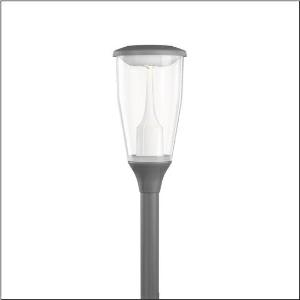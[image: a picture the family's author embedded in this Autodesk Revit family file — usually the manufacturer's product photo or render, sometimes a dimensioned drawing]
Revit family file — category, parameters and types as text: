
# Revit family: dl_11_iq___p1_0a_5xa5575lf14h000022_ea02
name_source: partatom
category: Lighting Fixtures
units: mm (PartAtom-declared; Revit-internal decimal feet)

## family parameters
Cut with Voids When Loaded = No
Host = Face
Light Source = No
Part Type = Normal
Room Calculation Point = No
Round Connector Dimension = Use Diameter
Shared = No

## types (1)
- --- (1 x LED, 1530 lm, 10 W, 4000K)
    Apparent Load = 10 VA
    CIE Flux Codes = 34 63 91 95 100
    Color Rendering = 70
    Color Temperature = 4000K
    Default Elevation = 1800 mm
    Description = DL 11 iQ, mast luminaire, Module 540 iQ-SR, primary light control with 3 zone facetted reflector, of plastic, silver coated, highly specular, structured, primary optical cover: cover, of PMMA, transparent, light distribution: P1.0a, light emission: direct distribution, primary light characteristic: asymmetric, installation type: post-top, LED, High Power LED, light colour: 740, colour temperature: 4000K, control: Street-Remote, Auto-Match, Temp-Guard, Lumen-Switch, Night-Set, Smart-Wire, Light-Fading, Desk-Remote (wireless, voltage-free reading and setting of iQ features in the workshop via application-optimized NFC function/RFID function), optimised constant luminous flux control (CLO 2.0), mains connection: 220..240V, AC, 50/60Hz, connection cable pre-assembled, cable length: 5,5m, start of lifetime: 10W, end of service life: 10W, luminaire housing, upper part, of diecast aluminium, coated, Siteco® metallic grey (DB 702S), spigot size: 76mm (post-top), post-top mast mounting element, of diecast aluminium, coated, Siteco® metallic grey (DB 702S), Module 540 iQ-SR, traffic white (RAL 9016), equipment: standard, protection rating (complete): IP66, insulation class (complete): insulation class II (safety insulation), certification: CE, ENEC, ENEC+, VDE, packaging unit: 1 piece

Light Distribution: P1.0a
    Height = 665 mm
    Lamp = 1 x LED
    Lamp Light Flux = 1530 lm
    Lamp Power = 10 W
    Lamp count = 1
    Length = 334 mm
    Luminous efficacy = 153 lm/W
    Manufacturer = Siteco
    ModVariant = No
    Model = 5XA5575LF14H000022
    Number of Poles = 1
    OnlyDefault = Yes
    Power Factor = 1
    Product Name = DL 11 iQ | P1.0a
    Product group = mast luminaire | pylon top
    ProductGroupID = 6100
    Protection Class = Protection class II
    Protection Degree = IP 66
    RLX_Detail_Level = 1
    RLX_Emergency_Light_Flux = 0 lm
    RLX_Emergency_Type = 0
    RLX_Emergency_Type_DB = No
    RlxData = <blob elided: 108765 chars, md5=7b79821b>
    Socket = socket
    Standby Power = 0 W
    System Light Flux = 1530 lm
    System Power = 10 W
    Type Comments = factory setting: luminous flux: 100 % | dim-lin: 254 | 401 mA
    Type Image = l_1258354.jpg
    URL = http://relux.com
    VarID = @adj_024117
    Voltage = 0 V
    Weight = 0.00 kg
    Width = 0 mm  [stored 0 ft]

note: [stored X ft] marks values corroborated as IEEE doubles in the binary element streams (Revit-internal decimal feet)

## geometry (parser evidence)
native form markers: Blend x4, Sweep x11
no freeform markers — native parametric forms only
